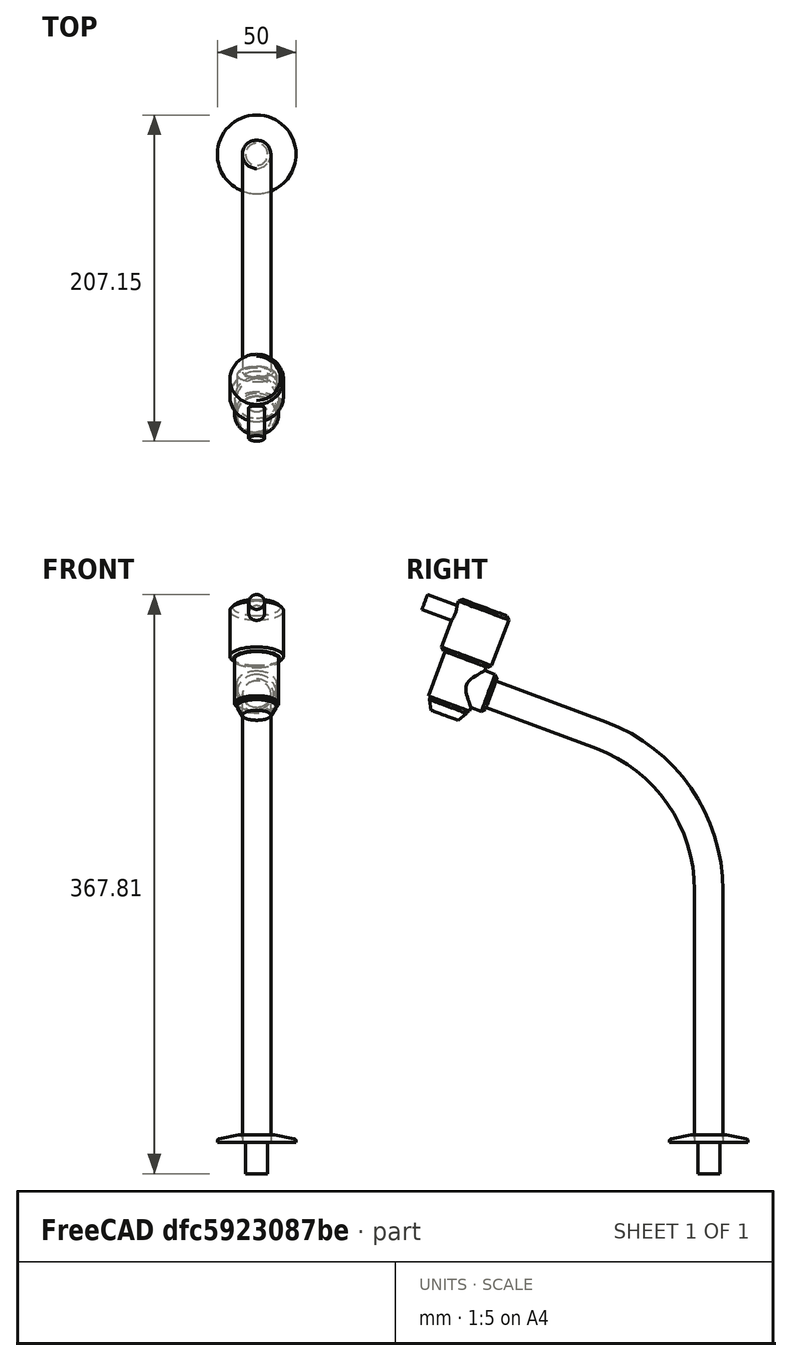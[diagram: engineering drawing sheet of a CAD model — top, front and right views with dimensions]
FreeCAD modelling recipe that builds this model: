
FCSTD DOCUMENT  (FreeCAD 1.0R38641 +468 (Git))
Label: Faucet_Lorenzetti_Banheiro
License: All rights reserved
objects: Part::Feature×1, Part::FeaturePython×1
note: 2 computed .brp shape members not serialized (recipe doc carries the construction recipe); baked Part::Feature solids carry a one-line shape summary decoded from their .brp

FEATURE [Part::Feature] Compound  label="Faucet_Lorenzetti_Banheiro"
  Placement = pos=(0,0,0) rot=(0.57735,0.57735,0.57735;2.0944rad)
  shape: bbox 54.12 x 209.2 x 367.8 mm, 46 faces, 3 solids (baked)
FEATURE [Part::FeaturePython] Component  label="Faucet_Lorenzetti_Banheiro001"  # Arch/BIM 22 (typed FeaturePython)
  Base = -> Compound
  HorizontalArea = 0
  IfcData = attributes={"GlobalId": {"name": "GlobalId", "type": "IfcGloballyUniqueId", "is_enum": false, "enum_values": []}, "Description": {"... (+538 chars omitted),+1 more (map truncated)
  IfcType = 22
  MoveBase = false
  MoveWithHost = false
  PerimeterLength = 0
  Placement = pos=(0,0,0) rot=(0.57735,0.57735,0.57735;2.0944rad)
  VerticalArea = 0
